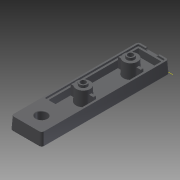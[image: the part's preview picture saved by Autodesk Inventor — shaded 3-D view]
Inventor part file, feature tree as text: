
AUTODESK INVENTOR PART (.ipt)
format: ipt  version: 2013 (Build 170138000, 138)  size: 420,864 bytes
history: native  units: in
note: dims shown in document units (in); Inventor stores cm internally (conversion verified against a paired STEP export)
features: sketch x12, extrude x10, fillet x7, projected_geometry x5, hole x2, plane x2, mirror x1, pattern_linear x1, other x1
ambient origin geometry x8: Origin, YZ Plane, XZ Plane, XY Plane, X Axis, Y Axis, Z Axis, Center Point
bodies: Solid1 (feature_tree)
feature tree (41):
  extrude  "Extrusion1"  Depth=2.026in
  hole  "Hole1"  [1 undecoded]
  extrude  "Extrusion2"  Depth=0.138in
  fillet  "Fillet1"  Radius=0.014in
  extrude  "Extrusion3"  Depth=0.02in
  extrude  "Extrusion4"  Depth=0.027in
  extrude  "Extrusion5"  Depth=0.028in
  extrude  "Extrusion7"  Depth=0.03in
  extrude  "Extrusion8"  Depth=0.03in
  fillet  "Fillet2"  Radius=0.008in
  plane  "Work Plane1"
  mirror  "Mirror1"
  pattern_linear  "Rectangular Pattern2"  Spacing1=0.228in  [1 undecoded]
  fillet  "Fillet3"  Radius=0.228in
  extrude  "Extrusion9"  Depth=0.224in
  hole  "Hole2"  [1 undecoded]
  extrude  "Extrusion10"  Depth=0.0185in
  fillet  "Fillet4"  Radius=0.224in
  fillet  "Fillet5"  Radius=0.002in
  fillet  "Fillet6"  Radius=0.047in
  plane  "Work Plane4"
  extrude  "Extrusion11"  Depth=0.012in
  fillet  "Fillet7"  Radius=0.014in
  sketch  "Sketch1"  dims[d3=0.5in d4=2.026in]
  sketch  "Sketch2"  dims[d6=0.197in d7=-0.0206in d8=0.25in]
  sketch  "Sketch3"  dims[d9=0.25in]
  sketch  "Sketch4"  dims[d10=0.171in d11=0.75in d12=0.375in d13=0.25in d14=0.5635in d15=1.0in d16=0.8108in d17=0.138in d18=-0.0069in d19=0.014in]
  sketch  "Sketch5"  dims[d20=0.027in d21=0.02in]
  sketch  "Sketch6"  dims[d22=0.027in d23=0.027in]
  sketch  "Sketch7"  dims[d24=1.479in d25=0.028in d26=-0.0034in]
  projected_geometry  "Projected Loop1"
  sketch  "Sketch8"  dims[d28=0.03in d29=0.03in]
  sketch  "Sketch9"  dims[d30=0.03in d31=0.03in d32=0.008in]
  projected_geometry  "Projected Loop2"
  sketch  "Sketch10"  dims[d33=0.11in d34=-0.0034in]
  projected_geometry  "Projected Loop3"
  sketch  "Sketch11"  dims[d35=0.656in]
  other  "Work Axis1"
  sketch  "Sketch14"  dims[d36=0.748in d37=0.228in d38=0.228in d39=0.224in d40=-0.0069in d41=0.037in d42=0.0185in d45=0.224in d46=0.0034in d47=0.002in d48=0.047in d49=0.0034in d50=0.012in d54=0.014in d55=0.122in d56=0.122in d57=0.039in d58=-0.0069in d59=0.083in d60=0.75in d61=0.375in d62=0.25in d63=0.5635in d64=1.0in d65=0.8108in d66=0.157in d67=0.224in d68=0.0in d69=0.014in d70=0.012in d71=0.7874in d73=0.748in d74=0.039in d75=90.0deg d76=0.028in d77=0.197in d78=1.0in d79=0.0in d80=0.031in]
  projected_geometry  "Projected Loop4"
  projected_geometry  "Project Cut Edges3"
note: 3 required parameter values undecoded (feature->parameter linkage not recoverable at this tier; creation-order binding heuristic only, values carry confidence <= 0.55)
